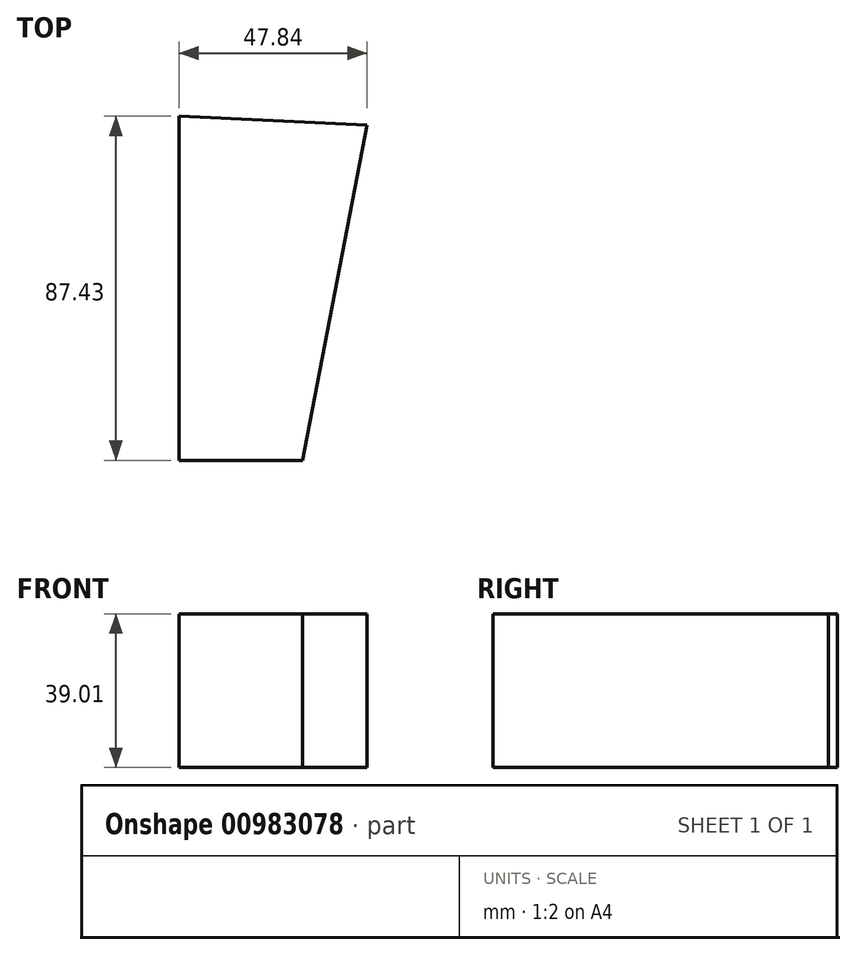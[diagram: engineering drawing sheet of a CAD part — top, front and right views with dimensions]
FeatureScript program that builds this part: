
annotation { "Feature Type Name" : "Feature", "Feature Type Description" : "" }
export const myFeature = defineFeature(function(context is Context, id is Id, definition is map)
    precondition{}
    {
        {
            var Q0;
            Q0=qCreatedBy(makeId("Top.planeOp"),FACE);
            var sketch = newSketch(context, id + "F0", { "sketchPlane" : qUnion([Q0])});
            skLineSegment(sketch, "E0", {"start": v(47.84, 45.14) * mm, "end": v(31.35, -40.04) * mm});
            skLineSegment(sketch, "E1", {"start": v(31.35, -40.04) * mm, "end": v(0, -40.04) * mm});
            skLineSegment(sketch, "E2", {"start": v(0, 47.4) * mm, "end": v(47.84, 45.14) * mm});
            skLineSegment(sketch, "E3", {"start": v(0, 47.4) * mm, "end": v(0, -40.04) * mm});
            skSolve(sketch);
        }
        {
            var Q0;
            Q0 = qSketchRegion(id + "F0", true);
            extrude(context, id + "F1", {"entities" : qUnion([Q0]), "depth" : 39 * mm, "offsetDistance" : 25.4 * mm});
        }
    });
